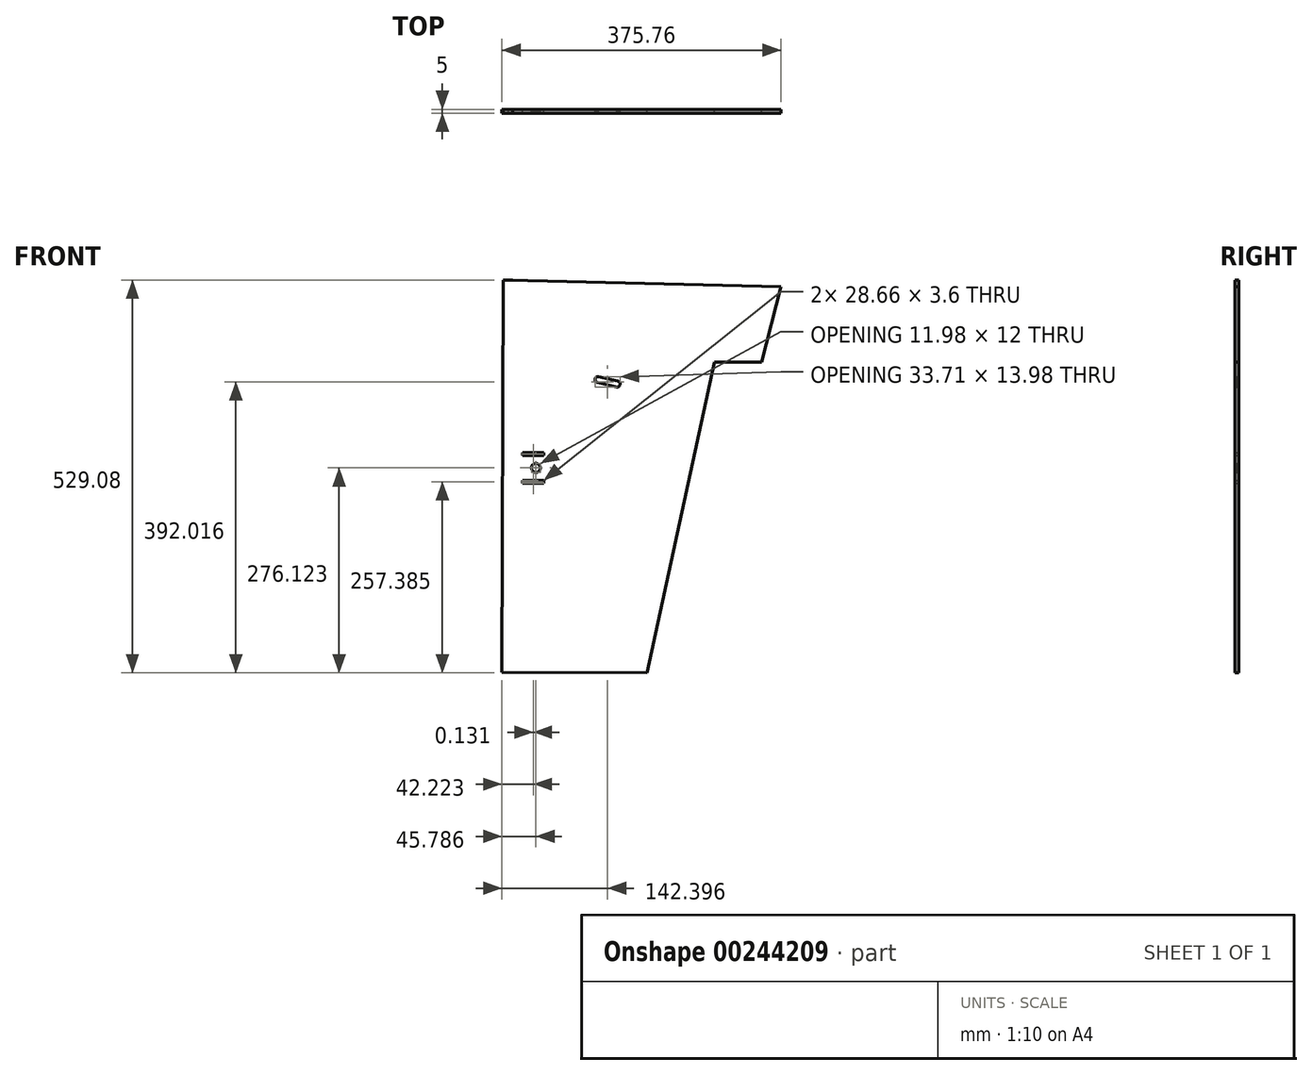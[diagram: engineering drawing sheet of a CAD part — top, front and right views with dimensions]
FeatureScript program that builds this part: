
annotation { "Feature Type Name" : "Feature", "Feature Type Description" : "" }
export const myFeature = defineFeature(function(context is Context, id is Id, definition is map)
    precondition{}
    {
        {
            var Q0;
            Q0=qCreatedBy(makeId("Front.planeOp"),FACE);
            var sketch = newSketch(context, id + "F0", { "sketchPlane" : qUnion([Q0])});
            skLineSegment(sketch, "E0", {"start": v(-173.5, 264.36) * mm, "end": v(-186.03, 264.54) * mm});
            skLineSegment(sketch, "E1", {"start": v(-186.03, 264.54) * mm, "end": v(-179.03, 264.37) * mm});
            skLineSegment(sketch, "E2", {"start": v(-179.03, 264.37) * mm, "end": v(-173.5, 264.36) * mm});
            skLineSegment(sketch, "E3", {"start": v(161.87, 153.86) * mm, "end": v(187.88, 255.6) * mm});
            skLineSegment(sketch, "E4", {"start": v(187.88, 255.6) * mm, "end": v(-179.03, 264.37) * mm});
            skLineSegment(sketch, "E5", {"start": v(-179.03, 264.37) * mm, "end": v(-186.03, 264.54) * mm});
            skLineSegment(sketch, "E6", {"start": v(-186.03, 264.54) * mm, "end": v(-187.88, -263.86) * mm});
            skLineSegment(sketch, "E7", {"start": v(-187.88, -263.86) * mm, "end": v(7.56, -264.54) * mm});
            skLineSegment(sketch, "E8", {"start": v(7.56, -264.54) * mm, "end": v(98.7, 154.08) * mm});
            skLineSegment(sketch, "E9", {"start": v(98.7, 154.08) * mm, "end": v(118.59, 154.01) * mm});
            skLineSegment(sketch, "E10", {"start": v(118.59, 154.01) * mm, "end": v(161.87, 153.86) * mm});
            skLineSegment(sketch, "E11", {"start": v(-159.99, -8.85) * mm, "end": v(-159.98, -5.35) * mm});
            skLineSegment(sketch, "E12", {"start": v(-159.98, -5.35) * mm, "end": v(-131.33, -5.45) * mm});
            skLineSegment(sketch, "E13", {"start": v(-131.33, -5.45) * mm, "end": v(-131.34, -8.95) * mm});
            skLineSegment(sketch, "E14", {"start": v(-131.34, -8.95) * mm, "end": v(-159.99, -8.85) * mm});
            skLineSegment(sketch, "E15", {"start": v(-159.86, 28.64) * mm, "end": v(-159.84, 32.14) * mm});
            skLineSegment(sketch, "E16", {"start": v(-159.84, 32.14) * mm, "end": v(-131.2, 32.04) * mm});
            skLineSegment(sketch, "E17", {"start": v(-131.2, 32.04) * mm, "end": v(-131.2, 28.54) * mm});
            skLineSegment(sketch, "E18", {"start": v(-131.2, 28.54) * mm, "end": v(-159.86, 28.64) * mm});
            skLineSegment(sketch, "E19", {"start": v(-147.98, 12.73) * mm, "end": v(-147.8, 13.46) * mm});
            skLineSegment(sketch, "E20", {"start": v(-147.8, 13.46) * mm, "end": v(-147.51, 14.16) * mm});
            skLineSegment(sketch, "E21", {"start": v(-147.51, 14.16) * mm, "end": v(-147.15, 14.82) * mm});
            skLineSegment(sketch, "E22", {"start": v(-147.15, 14.82) * mm, "end": v(-146.7, 15.42) * mm});
            skLineSegment(sketch, "E23", {"start": v(-146.7, 15.42) * mm, "end": v(-146.19, 15.97) * mm});
            skLineSegment(sketch, "E24", {"start": v(-146.19, 15.97) * mm, "end": v(-145.6, 16.45) * mm});
            skLineSegment(sketch, "E25", {"start": v(-145.6, 16.45) * mm, "end": v(-144.97, 16.85) * mm});
            skLineSegment(sketch, "E26", {"start": v(-144.97, 16.85) * mm, "end": v(-144.28, 17.17) * mm});
            skLineSegment(sketch, "E27", {"start": v(-144.28, 17.17) * mm, "end": v(-143.57, 17.4) * mm});
            skLineSegment(sketch, "E28", {"start": v(-143.57, 17.4) * mm, "end": v(-142.83, 17.54) * mm});
            skLineSegment(sketch, "E29", {"start": v(-142.83, 17.54) * mm, "end": v(-142.07, 17.58) * mm});
            skLineSegment(sketch, "E30", {"start": v(-142.07, 17.58) * mm, "end": v(-141.32, 17.53) * mm});
            skLineSegment(sketch, "E31", {"start": v(-141.32, 17.53) * mm, "end": v(-140.58, 17.39) * mm});
            skLineSegment(sketch, "E32", {"start": v(-140.58, 17.39) * mm, "end": v(-139.87, 17.15) * mm});
            skLineSegment(sketch, "E33", {"start": v(-139.87, 17.15) * mm, "end": v(-139.19, 16.83) * mm});
            skLineSegment(sketch, "E34", {"start": v(-139.19, 16.83) * mm, "end": v(-138.55, 16.42) * mm});
            skLineSegment(sketch, "E35", {"start": v(-138.55, 16.42) * mm, "end": v(-137.97, 15.94) * mm});
            skLineSegment(sketch, "E36", {"start": v(-137.97, 15.94) * mm, "end": v(-137.46, 15.4) * mm});
            skLineSegment(sketch, "E37", {"start": v(-137.46, 15.4) * mm, "end": v(-137.02, 14.78) * mm});
            skLineSegment(sketch, "E38", {"start": v(-137.02, 14.78) * mm, "end": v(-136.66, 14.12) * mm});
            skLineSegment(sketch, "E39", {"start": v(-136.66, 14.12) * mm, "end": v(-136.38, 13.42) * mm});
            skLineSegment(sketch, "E40", {"start": v(-136.38, 13.42) * mm, "end": v(-136.2, 12.69) * mm});
            skLineSegment(sketch, "E41", {"start": v(-136.2, 12.69) * mm, "end": v(-136.1, 11.94) * mm});
            skLineSegment(sketch, "E42", {"start": v(-136.1, 11.94) * mm, "end": v(-136.1, 11.19) * mm});
            skLineSegment(sketch, "E43", {"start": v(-136.1, 11.19) * mm, "end": v(-136.2, 10.44) * mm});
            skLineSegment(sketch, "E44", {"start": v(-136.2, 10.44) * mm, "end": v(-136.4, 9.7) * mm});
            skLineSegment(sketch, "E45", {"start": v(-136.4, 9.7) * mm, "end": v(-136.67, 9) * mm});
            skLineSegment(sketch, "E46", {"start": v(-136.67, 9) * mm, "end": v(-137.04, 8.35) * mm});
            skLineSegment(sketch, "E47", {"start": v(-137.04, 8.35) * mm, "end": v(-137.48, 7.74) * mm});
            skLineSegment(sketch, "E48", {"start": v(-137.48, 7.74) * mm, "end": v(-138, 7.2) * mm});
            skLineSegment(sketch, "E49", {"start": v(-138, 7.2) * mm, "end": v(-138.58, 6.72) * mm});
            skLineSegment(sketch, "E50", {"start": v(-138.58, 6.72) * mm, "end": v(-139.22, 6.31) * mm});
            skLineSegment(sketch, "E51", {"start": v(-139.22, 6.31) * mm, "end": v(-139.9, 6) * mm});
            skLineSegment(sketch, "E52", {"start": v(-139.9, 6) * mm, "end": v(-140.62, 5.77) * mm});
            skLineSegment(sketch, "E53", {"start": v(-140.62, 5.77) * mm, "end": v(-141.36, 5.63) * mm});
            skLineSegment(sketch, "E54", {"start": v(-141.36, 5.63) * mm, "end": v(-142.12, 5.58) * mm});
            skLineSegment(sketch, "E55", {"start": v(-142.12, 5.58) * mm, "end": v(-142.87, 5.63) * mm});
            skLineSegment(sketch, "E56", {"start": v(-142.87, 5.63) * mm, "end": v(-143.6, 5.78) * mm});
            skLineSegment(sketch, "E57", {"start": v(-143.6, 5.78) * mm, "end": v(-144.32, 6.01) * mm});
            skLineSegment(sketch, "E58", {"start": v(-144.32, 6.01) * mm, "end": v(-145, 6.33) * mm});
            skLineSegment(sketch, "E59", {"start": v(-145, 6.33) * mm, "end": v(-145.64, 6.74) * mm});
            skLineSegment(sketch, "E60", {"start": v(-145.64, 6.74) * mm, "end": v(-146.22, 7.22) * mm});
            skLineSegment(sketch, "E61", {"start": v(-146.22, 7.22) * mm, "end": v(-146.73, 7.77) * mm});
            skLineSegment(sketch, "E62", {"start": v(-146.73, 7.77) * mm, "end": v(-147.17, 8.39) * mm});
            skLineSegment(sketch, "E63", {"start": v(-147.17, 8.39) * mm, "end": v(-147.53, 9.05) * mm});
            skLineSegment(sketch, "E64", {"start": v(-147.53, 9.05) * mm, "end": v(-147.8, 9.75) * mm});
            skLineSegment(sketch, "E65", {"start": v(-147.8, 9.75) * mm, "end": v(-148, 10.48) * mm});
            skLineSegment(sketch, "E66", {"start": v(-148, 10.48) * mm, "end": v(-148.08, 11.23) * mm});
            skLineSegment(sketch, "E67", {"start": v(-148.08, 11.23) * mm, "end": v(-148.08, 11.98) * mm});
            skLineSegment(sketch, "E68", {"start": v(-148.08, 11.98) * mm, "end": v(-147.98, 12.73) * mm});
            skLineSegment(sketch, "E69", {"start": v(-33.26, 120.52) * mm, "end": v(-59.12, 126.55) * mm});
            skLineSegment(sketch, "E70", {"start": v(-59.12, 126.55) * mm, "end": v(-60.1, 126.88) * mm});
            skLineSegment(sketch, "E71", {"start": v(-60.1, 126.88) * mm, "end": v(-60.96, 127.45) * mm});
            skLineSegment(sketch, "E72", {"start": v(-60.96, 127.45) * mm, "end": v(-61.65, 128.22) * mm});
            skLineSegment(sketch, "E73", {"start": v(-61.65, 128.22) * mm, "end": v(-62.12, 129.14) * mm});
            skLineSegment(sketch, "E74", {"start": v(-62.12, 129.14) * mm, "end": v(-62.34, 130.15) * mm});
            skLineSegment(sketch, "E75", {"start": v(-62.34, 130.15) * mm, "end": v(-62.3, 131.19) * mm});
            skLineSegment(sketch, "E76", {"start": v(-62.3, 131.19) * mm, "end": v(-61.98, 132.17) * mm});
            skLineSegment(sketch, "E77", {"start": v(-61.98, 132.17) * mm, "end": v(-61.42, 133.05) * mm});
            skLineSegment(sketch, "E78", {"start": v(-61.42, 133.05) * mm, "end": v(-60.66, 133.75) * mm});
            skLineSegment(sketch, "E79", {"start": v(-60.66, 133.75) * mm, "end": v(-59.75, 134.23) * mm});
            skLineSegment(sketch, "E80", {"start": v(-59.75, 134.23) * mm, "end": v(-58.74, 134.46) * mm});
            skLineSegment(sketch, "E81", {"start": v(-58.74, 134.46) * mm, "end": v(-57.7, 134.43) * mm});
            skLineSegment(sketch, "E82", {"start": v(-57.7, 134.43) * mm, "end": v(-31.85, 128.4) * mm});
            skLineSegment(sketch, "E83", {"start": v(-31.85, 128.4) * mm, "end": v(-30.87, 128.07) * mm});
            skLineSegment(sketch, "E84", {"start": v(-30.87, 128.07) * mm, "end": v(-30, 127.5) * mm});
            skLineSegment(sketch, "E85", {"start": v(-30, 127.5) * mm, "end": v(-29.32, 126.73) * mm});
            skLineSegment(sketch, "E86", {"start": v(-29.32, 126.73) * mm, "end": v(-28.85, 125.81) * mm});
            skLineSegment(sketch, "E87", {"start": v(-28.85, 125.81) * mm, "end": v(-28.63, 124.8) * mm});
            skLineSegment(sketch, "E88", {"start": v(-28.63, 124.8) * mm, "end": v(-28.68, 123.77) * mm});
            skLineSegment(sketch, "E89", {"start": v(-28.68, 123.77) * mm, "end": v(-29, 122.78) * mm});
            skLineSegment(sketch, "E90", {"start": v(-29, 122.78) * mm, "end": v(-29.55, 121.9) * mm});
            skLineSegment(sketch, "E91", {"start": v(-29.55, 121.9) * mm, "end": v(-30.3, 121.2) * mm});
            skLineSegment(sketch, "E92", {"start": v(-30.3, 121.2) * mm, "end": v(-31.22, 120.72) * mm});
            skLineSegment(sketch, "E93", {"start": v(-31.22, 120.72) * mm, "end": v(-32.23, 120.49) * mm});
            skLineSegment(sketch, "E94", {"start": v(-32.23, 120.49) * mm, "end": v(-33.26, 120.52) * mm});
            skSolve(sketch);
        }
        {
            var Q0;
            Q0 = qSketchRegion(id + "F0", true);
            extrude(context, id + "F1", {"entities" : qUnion([Q0]), "depth" : 5 * mm});
        }
    });
